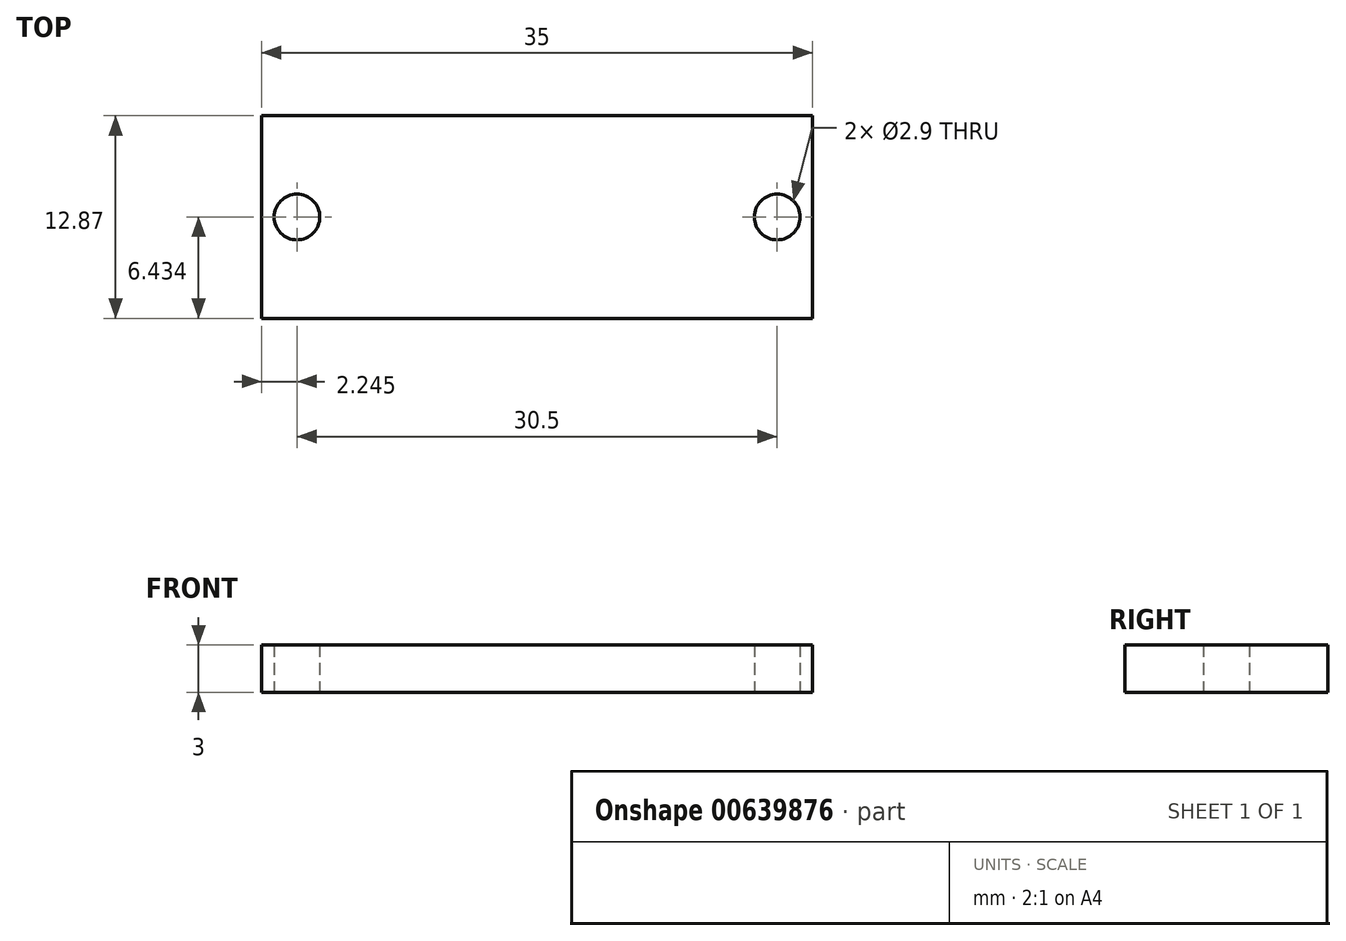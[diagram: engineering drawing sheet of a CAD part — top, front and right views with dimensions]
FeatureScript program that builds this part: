
annotation { "Feature Type Name" : "Feature", "Feature Type Description" : "" }
export const myFeature = defineFeature(function(context is Context, id is Id, definition is map)
    precondition{}
    {
        {
            var Q0;
            Q0=qCreatedBy(makeId("Top.planeOp"),FACE);
            var sketch = newSketch(context, id + "F0", { "sketchPlane" : qUnion([Q0])});
            skLineSegment(sketch, "E0.0", {"start": v(-56, -23.7) * mm, "end": v(-21, -23.7) * mm, "construction": true});
            skLineSegment(sketch, "E1", {"start": v(-53.75, -6.2) * mm, "end": v(-53.75, -41.2) * mm, "construction": true});
            skLineSegment(sketch, "E2", {"start": v(-23.25, -6.2) * mm, "end": v(-23.25, -41.3) * mm, "construction": true});
            skCircle(sketch, "E3", {"center": v(-53.75, -23.7) * mm, "radius": 1.45 * mm});
            skCircle(sketch, "E4", {"center": v(-23.25, -23.7) * mm, "radius": 1.45 * mm});
            skLineSegment(sketch, "E5.bottom", {"start": v(-21, -17.26) * mm, "end": v(-56, -17.26) * mm});
            skLineSegment(sketch, "E5.top", {"start": v(-21, -30.13) * mm, "end": v(-56, -30.13) * mm});
            skLineSegment(sketch, "E5.left", {"start": v(-21, -17.26) * mm, "end": v(-21, -30.13) * mm});
            skLineSegment(sketch, "E5.right", {"start": v(-56, -17.26) * mm, "end": v(-56, -30.13) * mm});
            skPoint(sketch, "E5.middle", {"position": v(-38.5, -23.7) * mm});
            skSolve(sketch);
        }
        {
            var Q0;
            Q0=makeQuery(id+"F0.imprint","IMPRINT",FACE,{"disambiguationData":[TD([[makeQuery(id+"F0.imprint","IMPRINT",EDGE,{"derivedFrom":sQuery(id+"F0.wireOp",EDGE,"E3")}),-1.0]])]});
            extrude(context, id + "F1", {"entities" : qUnion([Q0]), "depth" : 3 * mm, "offsetDistance" : 25 * mm});
        }
    });
